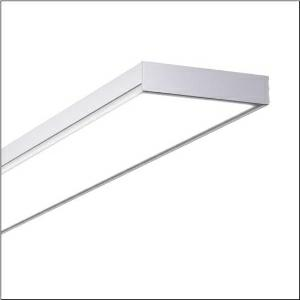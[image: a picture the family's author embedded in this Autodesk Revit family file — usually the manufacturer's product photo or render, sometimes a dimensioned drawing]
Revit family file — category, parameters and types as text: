
# Revit family: apollon_31_surface_51mp26wm2441ea
name_source: partatom
category: Lighting Fixtures
units: mm (PartAtom-declared; Revit-internal decimal feet)

## family parameters
Cut with Voids When Loaded = No
Host = Face
Light Source = No
Part Type = Normal
Room Calculation Point = No
Round Connector Dimension = Use Diameter
Shared = No

## types (1)
- Apollon 31 Surface (1 x LED, 4600 lm, 33 W, 4000K)
    Apparent Load = 33 VA
    CIE Flux Codes = 61 87 97 97 100
    Color Rendering = 80
    Color Temperature = 4000K
    Default Elevation = 1800 mm
    Description = Apollon 31 Surface, office luminaire, primary optical cover: micro prismatic cover, of PMMA, light emission: direct distribution, primary light characteristic: symmetric, installation type: surface-mounted, LED, rated luminous flux: 4.600lm, luminous efficacy: 139lm/W, light colour: 840, colour temperature: 4000K, control gear: ON/OFF Multilumen, with terminal, 3-pole, mains connection: 220..240V, AC, 50/60Hz, rated input power: 33W, housing, of sheet steel, coated, metallic grey (RAL 9006), length: 1.545mm, width: 200mm, height: 44mm, protection rating (complete): IP20, protection rating (on room side): IP40, protection rating (lamp compartment, on room side): IP40, insulation class (complete): insulation class I (protective earthing), certification: CE, ENEC, UKCA, impact resistance: IK02, permissible operating ambient temperature: -20..+40°C, packaging unit: 1 piece
    Height = 44 mm
    Lamp = 1 x LED
    Lamp Light Flux = 4600 lm
    Lamp Power = 33 W
    Lamp count = 1
    Length = 1545 mm
    Luminous efficacy = 139 lm/W
    Manufacturer = Siteco
    ModVariant = No
    Model = 51MP26WM2441EA
    Mounting Place = Ceiling
    Mounting Type = Surface mounted
    Number of Poles = 1
    OnlyDefault = Yes
    Power Factor = 1
    Product Name = Apollon 31 Surface
    Product group = office luminaire | ceiling mounted
    ProductGroupID = 301
    Protection Class = Protection class I
    Protection Degree = IP 20
    RLX_Detail_Level = 1
    RLX_Emergency_Light_Flux = 0 lm
    RLX_Emergency_Type = 0
    RLX_Emergency_Type_DB = No
    RlxData = <blob elided: 24129 chars, md5=8651b0c8>
    Socket = socket
    Standby Power = 0 W
    System Light Flux = 4600 lm
    System Power = 33 W
    Type Comments = Product without accessories
    Type Image = l_1313654.jpg
    URL = http://relux.com
    VarID = ---
    Voltage = 0 V
    Weight = 0.00 kg
    Width = 200 mm  [stored 0.656168 ft]

note: [stored X ft] marks values corroborated as IEEE doubles in the binary element streams (Revit-internal decimal feet)

## geometry (parser evidence)
native form markers: Blend x4, Sweep x11
no freeform markers — native parametric forms only
